# Revit family: 6180 series
name_source: partatom
category: Mechanical Equipment
revit_build: Autodesk Revit 2013 (Build: 20120221_2030(x64)
units: mm (PartAtom-declared; Revit-internal decimal feet)

## types (96) — shared parameters
Assembly Code = D2010900
Default Elevation = 0"
Description = Commercial Effluent Pumps
Discharge Height = 6"
Height = 21 3/16"
Hertz = 60
Impeller Type = Bronze Vortex
Installation Type = Floor Mounted
Length = 12 3/4"
Manufacturer = Zoeller
Masterformat Number = 33 36 16
Masterformat Title = Utility Septic Tank Effluent Pumps
Material = Cast Iron-Zoeller-Powder Coated Epoxy
Max. Water Temp. = 130 °F
Min. Recommended Fluid Level = 10"
Moisture Sensor (Optional) = Requires a circuit in control panel
Motor Design Letter = NEMA B
Motor Shaft = 416 S.S.
Motor Thermal Shutoff (Single Phase Only) = Thermal Overload Protector With Automatic Reset.
Motor Type = Submersible
O-Rings and Cover Gasket = Viton
Omniclass Table 23 Code = 23.60.30.21
Omniclass Table 23 Title = Pumps
Operation = Non-Automatic
Price = Prices may vary. Please consult Manufacturer Representative for most up-to-date price list.
Product Page URL = http://www.zoellerengprod.com
RPM = 3450
Service Factor = 1.15
Shaft Seal Lower (Options) = Silicon Carbide/Silicon Carbide
Shaft Seal Lower Standard = Silicon Carbide/Carbon
Shaft Seal Upper (Options) = Silicon Carbide/Carbon, Silicon Carbide/Silicon Carbide
Shaft Seal Upper Standard = Carbon/Ceramic
Shipping Weight = 89-94 lbs
Type SOW Power Cord Length = 300"
URL = http://www.zoellerengprod.com
Warranty Information = 36 Months (Limited)
Waste Connection = Yes
Width = 8"

## per-type parameters (varying)
| type | Apparent power | Discharge Diameter | Discharge Radius | Flange | Flange Visibility Height | Flow 6185 @ 30', 6186, 6188, 6189 @ 5' | Full Load Amps | Insulation | Lead Wires Insulation | Locked Rotor Amps (Voltage Dependant) | Max. Stator Temp. | Maximum Head | Minimum Head | Model | Motor | No Flange | Phase | Type | Void Visibility | Voltage |
| 6185-1.5" 200V 1Ph | 2300 VA | 1-1/2" NPT | 3/4" | No | 5 1/2" | 85 GPM | 12 A | Class B | Class B | 26.9 | 266 °F | 876" | 360" | 6185-1.5" | 1 HP | Yes | 1 | Permanent Split Capacitor | 8 1/4" | 200 V |
| 6185-1.5" 208V 1Ph | 2392 VA | 1-1/2" NPT | 3/4" | No | 5 1/2" | 85 GPM | 12 A | Class B | Class B | 26.9 | 266 °F | 876" | 360" | 6185-1.5" | 1 HP | Yes | 1 | Permanent Split Capacitor | 8 1/4" | 208 V |
| 6185-1.5" 230V 1Ph | 2254 VA | 1-1/2" NPT | 3/4" | No | 5 1/2" | 85 GPM | 10 A | Class B | Class B | 19.0 | 266 °F | 876" | 360" | 6185-1.5" | 1 HP | Yes | 1 | Permanent Split Capacitor | 8 1/4" | 230 V |
| 6185-1.5" 200V 3Ph | 1500 VA | 1-1/2" NPT | 3/4" | No | 5 1/2" | 85 GPM | 8 A | Class B | Class B | 30.0 | 266 °F | 876" | 360" | 6185-1.5" | 1 HP | Yes | 3 | 3 Phase | 8 1/4" | 200 V |
| 6185-1.5" 208V 3Ph | 1560 VA | 1-1/2" NPT | 3/4" | No | 5 1/2" | 85 GPM | 8 A | Class B | Class B | 30.0 | 266 °F | 876" | 360" | 6185-1.5" | 1 HP | Yes | 3 | 3 Phase | 8 1/4" | 208 V |
| 6185-1.5" 230V 3Ph | 1702 VA | 1-1/2" NPT | 3/4" | No | 5 1/2" | 85 GPM | 7 A | Class B | Class B | 27.0 | 266 °F | 876" | 360" | 6185-1.5" | 1 HP | Yes | 3 | 3 Phase | 8 1/4" | 230 V |
| 6185-1.5" 460V 3Ph | 1702 VA | 1-1/2" NPT | 3/4" | No | 5 1/2" | 85 GPM | 4 A | Class B | Class B | 14.0 | 266 °F | 876" | 360" | 6185-1.5" | 1 HP | Yes | 3 | 3 Phase | 8 1/4" | 460 V |
| 6185-1.5" 575V 3Ph | 1898 VA | 1-1/2" NPT | 3/4" | No | 5 1/2" | 85 GPM | 3 A | Class B | Class B | 12.0 | 266 °F | 876" | 360" | 6185-1.5" | 1 HP | Yes | 3 | 3 Phase | 8 1/4" | 575 V |
| 6185-2" 200V 1Ph | 2300 VA | 2" NPT | 1" | Yes | 6" | 85 GPM | 12 A | Class B | Class B | 26.9 | 266 °F | 876" | 360" | 6185-2" | 1 HP | No | 1 | Permanent Split Capacitor | 3" | 200 V |
| 6185-2" 208V 1Ph | 2392 VA | 2" NPT | 1" | Yes | 6" | 85 GPM | 12 A | Class B | Class B | 26.9 | 266 °F | 876" | 360" | 6185-2" | 1 HP | No | 1 | Permanent Split Capacitor | 3" | 208 V |
| 6185-2" 230V 1Ph | 2254 VA | 2" NPT | 1" | Yes | 6" | 85 GPM | 10 A | Class B | Class B | 19.0 | 266 °F | 876" | 360" | 6185-2" | 1 HP | No | 1 | Permanent Split Capacitor | 3" | 230 V |
| 6185-2" 200V 3Ph | 1500 VA | 2" NPT | 1" | Yes | 6" | 85 GPM | 8 A | Class B | Class B | 30.0 | 266 °F | 876" | 360" | 6185-2" | 1 HP | No | 3 | 3 Phase | 3" | 200 V |
| 6185-2" 208V 3Ph | 1560 VA | 2" NPT | 1" | Yes | 6" | 85 GPM | 8 A | Class B | Class B | 30.0 | 266 °F | 876" | 360" | 6185-2" | 1 HP | No | 3 | 3 Phase | 3" | 208 V |
| 6185-2" 230V 3Ph | 1702 VA | 2" NPT | 1" | Yes | 6" | 85 GPM | 7 A | Class B | Class B | 27.0 | 266 °F | 876" | 360" | 6185-2" | 1 HP | No | 3 | 3 Phase | 3" | 230 V |
| 6185-2" 460V 3Ph | 1702 VA | 2" NPT | 1" | Yes | 6" | 85 GPM | 4 A | Class B | Class B | 14.0 | 266 °F | 876" | 360" | 6185-2" | 1 HP | No | 3 | 3 Phase | 3" | 460 V |
| 6185-2" 575V 3Ph | 1898 VA | 2" NPT | 1" | Yes | 6" | 85 GPM | 3 A | Class B | Class B | 12.0 | 266 °F | 876" | 360" | 6185-2" | 1 HP | No | 3 | 3 Phase | 3" | 575 V |
| 6185-3" 200V 1Ph | 2300 VA | 3" NPT | 1 1/2" | Yes | 6" | 85 GPM | 12 A | Class B | Class B | 26.9 | 266 °F | 876" | 360" | 6185-3" | 1 HP | No | 1 | Permanent Split Capacitor | 3" | 200 V |
| 6185-3" 208V 1Ph | 2392 VA | 3" NPT | 1 1/2" | Yes | 6" | 85 GPM | 12 A | Class B | Class B | 26.9 | 266 °F | 876" | 360" | 6185-3" | 1 HP | No | 1 | Permanent Split Capacitor | 3" | 208 V |
| 6185-3" 230V 1Ph | 2254 VA | 3" NPT | 1 1/2" | Yes | 6" | 85 GPM | 10 A | Class B | Class B | 19.0 | 266 °F | 876" | 360" | 6185-3" | 1 HP | No | 1 | Permanent Split Capacitor | 3" | 230 V |
| 6185-3" 200V 3Ph | 1500 VA | 3" NPT | 1 1/2" | Yes | 6" | 85 GPM | 8 A | Class B | Class B | 30.0 | 266 °F | 876" | 360" | 6185-3" | 1 HP | No | 3 | 3 Phase | 3" | 200 V |
| 6185-3" 208V 3Ph | 1560 VA | 3" NPT | 1 1/2" | Yes | 6" | 85 GPM | 8 A | Class B | Class B | 30.0 | 266 °F | 876" | 360" | 6185-3" | 1 HP | No | 3 | 3 Phase | 3" | 208 V |
| 6185-3" 230V 3Ph | 1702 VA | 3" NPT | 1 1/2" | Yes | 6" | 85 GPM | 7 A | Class B | Class B | 27.0 | 266 °F | 876" | 360" | 6185-3" | 1 HP | No | 3 | 3 Phase | 3" | 230 V |
| 6185-3" 460V 3Ph | 1702 VA | 3" NPT | 1 1/2" | Yes | 6" | 85 GPM | 4 A | Class B | Class B | 14.0 | 266 °F | 876" | 360" | 6185-3" | 1 HP | No | 3 | 3 Phase | 3" | 460 V |
| 6185-3" 575V 3Ph | 1898 VA | 3" NPT | 1 1/2" | Yes | 6" | 85 GPM | 3 A | Class B | Class B | 12.0 | 266 °F | 876" | 360" | 6185-3" | 1 HP | No | 3 | 3 Phase | 3" | 575 V |
| 6186-1.5" 200V 1Ph | 3440 VA | 1-1/2" NPT | 3/4" | No | 5 1/2" | 58 GPM | 17 A | Class F | Class F | 48.3 | 311 °F | 1368" | 60" | 6186-1.5" | 1-1/2 HP | Yes | 1 | Permanent Split Capacitor | 8 1/4" | 200 V |
| 6186-1.5" 208V 1Ph | 3578 VA | 1-1/2" NPT | 3/4" | No | 5 1/2" | 58 GPM | 17 A | Class F | Class F | 48.3 | 311 °F | 1368" | 60" | 6186-1.5" | 1-1/2 HP | Yes | 1 | Permanent Split Capacitor | 8 1/4" | 208 V |
| 6186-1.5" 230V 1Ph | 3151 VA | 1-1/2" NPT | 3/4" | No | 5 1/2" | 58 GPM | 14 A | Class F | Class F | 38.0 | 311 °F | 1368" | 60" | 6186-1.5" | 1-1/2 HP | Yes | 1 | Permanent Split Capacitor | 8 1/4" | 230 V |
| 6186-1.5" 200V 3Ph | 2060 VA | 1-1/2" NPT | 3/4" | No | 5 1/2" | 58 GPM | 10 A | Class F | Class F | 42.0 | 311 °F | 1368" | 60" | 6186-1.5" | 1-1/2 HP | Yes | 3 | 3 Phase | 8 1/4" | 200 V |
| 6186-1.5" 208V 3Ph | 2142 VA | 1-1/2" NPT | 3/4" | No | 5 1/2" | 58 GPM | 10 A | Class F | Class F | 42.0 | 311 °F | 1368" | 60" | 6186-1.5" | 1-1/2 HP | Yes | 3 | 3 Phase | 8 1/4" | 208 V |
| 6186-1.5" 230V 3Ph | 2254 VA | 1-1/2" NPT | 3/4" | No | 5 1/2" | 58 GPM | 10 A | Class F | Class F | 35.0 | 311 °F | 1368" | 60" | 6186-1.5" | 1-1/2 HP | Yes | 3 | 3 Phase | 8 1/4" | 230 V |
| 6186-1.5" 460V 3Ph | 2116 VA | 1-1/2" NPT | 3/4" | No | 5 1/2" | 58 GPM | 5 A | Class F | Class F | 18.0 | 311 °F | 1368" | 60" | 6186-1.5" | 1-1/2 HP | Yes | 3 | 3 Phase | 8 1/4" | 460 V |
| 6186-1.5" 575V 3Ph | 2070 VA | 1-1/2" NPT | 3/4" | No | 5 1/2" | 58 GPM | 4 A | Class F | Class F | 18.0 | 311 °F | 1368" | 60" | 6186-1.5" | 1-1/2 HP | Yes | 3 | 3 Phase | 8 1/4" | 575 V |
| 6186-2" 200V 1Ph | 3440 VA | 2" NPT | 1" | Yes | 6" | 58 GPM | 17 A | Class F | Class F | 48.3 | 311 °F | 1368" | 60" | 6186-2" | 1-1/2 HP | No | 1 | Permanent Split Capacitor | 3" | 200 V |
| 6186-2" 208V 1Ph | 3578 VA | 2" NPT | 1" | Yes | 6" | 58 GPM | 17 A | Class F | Class F | 48.3 | 311 °F | 1368" | 60" | 6186-2" | 1-1/2 HP | No | 1 | Permanent Split Capacitor | 3" | 208 V |
| 6186-2" 230V 1Ph | 3151 VA | 2" NPT | 1" | Yes | 6" | 58 GPM | 14 A | Class F | Class F | 38.0 | 311 °F | 1368" | 60" | 6186-2" | 1-1/2 HP | No | 1 | Permanent Split Capacitor | 3" | 230 V |
| 6186-2" 200V 3Ph | 2060 VA | 2" NPT | 1" | Yes | 6" | 58 GPM | 10 A | Class F | Class F | 42.0 | 311 °F | 1368" | 60" | 6186-2" | 1-1/2 HP | No | 3 | 3 Phase | 3" | 200 V |
| 6186-2" 208V 3Ph | 2142 VA | 2" NPT | 1" | Yes | 6" | 58 GPM | 10 A | Class F | Class F | 42.0 | 311 °F | 1368" | 60" | 6186-2" | 1-1/2 HP | No | 3 | 3 Phase | 3" | 208 V |
| 6186-2" 230V 3Ph | 2116 VA | 2" NPT | 1" | Yes | 6" | 58 GPM | 9 A | Class F | Class F | 35.0 | 311 °F | 1368" | 60" | 6186-2" | 1-1/2 HP | No | 3 | 3 Phase | 3" | 230 V |
| 6186-2" 460V 3Ph | 2116 VA | 2" NPT | 1" | Yes | 6" | 58 GPM | 5 A | Class F | Class F | 18.0 | 311 °F | 1368" | 60" | 6186-2" | 1-1/2 HP | No | 3 | 3 Phase | 3" | 460 V |
| 6186-2" 575V 3Ph | 2070 VA | 2" NPT | 1" | Yes | 6" | 58 GPM | 4 A | Class F | Class F | 18.0 | 311 °F | 1368" | 60" | 6186-2" | 1-1/2 HP | No | 3 | 3 Phase | 3" | 575 V |
| 6186-3" 200V 1Ph | 3440 VA | 3" NPT | 1 1/2" | Yes | 6" | 58 GPM | 17 A | Class F | Class F | 48.3 | 311 °F | 1368" | 60" | 6186-3" | 1-1/2 HP | No | 1 | Permanent Split Capacitor | 3" | 200 V |
| 6186-3" 208V 1Ph | 3578 VA | 3" NPT | 1 1/2" | Yes | 6" | 58 GPM | 17 A | Class F | Class F | 48.3 | 311 °F | 1368" | 60" | 6186-3" | 1-1/2 HP | No | 1 | Permanent Split Capacitor | 3" | 208 V |
| 6186-3" 230V 1Ph | 3151 VA | 3" NPT | 1 1/2" | Yes | 6" | 58 GPM | 14 A | Class F | Class F | 38.0 | 311 °F | 1368" | 60" | 6186-3" | 1-1/2 HP | No | 1 | Permanent Split Capacitor | 3" | 230 V |
| 6186-3" 200V 3Ph | 2060 VA | 3" NPT | 1 1/2" | Yes | 6" | 58 GPM | 10 A | Class F | Class F | 42.0 | 311 °F | 1368" | 60" | 6186-3" | 1-1/2 HP | No | 3 | 3 Phase | 3" | 200 V |
| 6186-3" 208V 3Ph | 2142 VA | 3" NPT | 1 1/2" | Yes | 6" | 58 GPM | 10 A | Class F | Class F | 42.0 | 311 °F | 1368" | 60" | 6186-3" | 1-1/2 HP | No | 3 | 3 Phase | 3" | 208 V |
| 6186-3" 230V 3Ph | 2116 VA | 3" NPT | 1 1/2" | Yes | 6" | 58 GPM | 9 A | Class F | Class F | 35.0 | 311 °F | 1368" | 60" | 6186-3" | 1-1/2 HP | No | 3 | 3 Phase | 3" | 230 V |
| 6186-3" 460V 3Ph | 2116 VA | 3" NPT | 1 1/2" | Yes | 6" | 58 GPM | 5 A | Class F | Class F | 18.0 | 311 °F | 1368" | 60" | 6186-3" | 1-1/2 HP | No | 3 | 3 Phase | 3" | 460 V |
| 6186-3" 575V 3Ph | 2070 VA | 3" NPT | 1 1/2" | Yes | 6" | 58 GPM | 4 A | Class F | Class F | 18.0 | 311 °F | 1368" | 60" | 6186-3" | 1-1/2 HP | No | 3 | 3 Phase | 3" | 575 V |
| 6188-1.5" 200V 1Ph | 3360 VA | 1-1/2" NPT | 3/4" | No | 5 1/2" | 145 GPM | 17 A | Class F | Class F | 48.3 | 311 °F | 1092" | 60" | 6188-1.5" | 1-1/2 HP | Yes | 1 | Permanent Split Capacitor | 8 1/4" | 200 V |
| 6188-1.5" 208V 1Ph | 3494 VA | 1-1/2" NPT | 3/4" | No | 5 1/2" | 145 GPM | 17 A | Class F | Class F | 48.3 | 311 °F | 1092" | 60" | 6188-1.5" | 1-1/2 HP | Yes | 1 | Permanent Split Capacitor | 8 1/4" | 208 V |
| 6188-1.5" 230V 1Ph | 3220 VA | 1-1/2" NPT | 3/4" | No | 5 1/2" | 145 GPM | 14 A | Class F | Class F | 38.0 | 311 °F | 1092" | 60" | 6188-1.5" | 1-1/2 HP | Yes | 1 | Permanent Split Capacitor | 8 1/4" | 230 V |
| 6188-1.5" 200V 3Ph | 2060 VA | 1-1/2" NPT | 3/4" | No | 5 1/2" | 145 GPM | 10 A | Class F | Class F | 42.0 | 311 °F | 1092" | 60" | 6188-1.5" | 1-1/2 HP | Yes | 3 | 3 Phase | 8 1/4" | 200 V |
| 6188-1.5" 208V 3Ph | 2142 VA | 1-1/2" NPT | 3/4" | No | 5 1/2" | 145 GPM | 10 A | Class F | Class F | 42.0 | 311 °F | 1092" | 60" | 6188-1.5" | 1-1/2 HP | Yes | 3 | 3 Phase | 8 1/4" | 208 V |
| 6188-1.5" 230V 3Ph | 2047 VA | 1-1/2" NPT | 3/4" | No | 5 1/2" | 145 GPM | 9 A | Class F | Class F | 35.0 | 311 °F | 1092" | 60" | 6188-1.5" | 1-1/2 HP | Yes | 3 | 3 Phase | 8 1/4" | 230 V |
| 6188-1.5" 460V 3Ph | 2116 VA | 1-1/2" NPT | 3/4" | No | 5 1/2" | 145 GPM | 5 A | Class F | Class F | 18.0 | 311 °F | 1092" | 60" | 6188-1.5" | 1-1/2 HP | Yes | 3 | 3 Phase | 8 1/4" | 460 V |
| 6188-1.5" 575V 3Ph | 2013 VA | 1-1/2" NPT | 3/4" | No | 5 1/2" | 145 GPM | 4 A | Class F | Class F | 18.0 | 311 °F | 1092" | 60" | 6188-1.5" | 1-1/2 HP | Yes | 3 | 3 Phase | 8 1/4" | 575 V |
| 6188-2" 200V 1Ph | 3360 VA | 2" NPT | 1" | Yes | 6" | 145 GPM | 17 A | Class F | Class F | 48.3 | 311 °F | 1092" | 60" | 6188-2" | 1-1/2 HP | No | 1 | Permanent Split Capacitor | 3" | 200 V |
| 6188-2" 208V 1Ph | 3494 VA | 2" NPT | 1" | Yes | 6" | 145 GPM | 17 A | Class F | Class F | 48.3 | 311 °F | 1092" | 60" | 6188-2" | 1-1/2 HP | No | 1 | Permanent Split Capacitor | 3" | 208 V |
| 6188-2" 230V 1Ph | 3220 VA | 2" NPT | 1" | Yes | 6" | 145 GPM | 14 A | Class F | Class F | 38 | 311 °F | 1092" | 60" | 6188-2" | 1-1/2 HP | No | 1 | Permanent Split Capacitor | 3" | 230 V |
| 6188-2" 200V 3Ph | 2060 VA | 2" NPT | 1" | Yes | 6" | 145 GPM | 10 A | Class F | Class F | 42.0 | 311 °F | 1092" | 60" | 6188-2" | 1-1/2 HP | No | 3 | 3 Phase | 3" | 200 V |
| 6188-2" 208V 3Ph | 2142 VA | 2" NPT | 1" | Yes | 6" | 145 GPM | 10 A | Class F | Class F | 42.0 | 311 °F | 1092" | 60" | 6188-2" | 1-1/2 HP | No | 3 | 3 Phase | 3" | 208 V |
| 6188-2" 230V 3Ph | 2047 VA | 2" NPT | 1" | Yes | 6" | 145 GPM | 9 A | Class F | Class F | 35.0 | 311 °F | 1092" | 60" | 6188-2" | 1-1/2 HP | No | 3 | 3 Phase | 3" | 230 V |
| 6188-2" 460V 3Ph | 2116 VA | 2" NPT | 1" | Yes | 6" | 145 GPM | 5 A | Class F | Class F | 18.0 | 311 °F | 1092" | 60" | 6188-2" | 1-1/2 HP | No | 3 | 3 Phase | 3" | 460 V |
| 6188-2" 575V 3Ph | 2013 VA | 2" NPT | 1" | Yes | 6" | 145 GPM | 4 A | Class F | Class F | 18.0 | 311 °F | 1092" | 60" | 6188-2" | 1-1/2 HP | No | 3 | 3 Phase | 3" | 575 V |
| 6188-3" 200V 1Ph | 3360 VA | 3" NPT | 1 1/2" | Yes | 6" | 145 GPM | 17 A | Class F | Class F | 48.3 | 311 °F | 1092" | 60" | 6188-3" | 1-1/2 HP | No | 1 | Permanent Split Capacitor | 3" | 200 V |
| 6188-3" 208V 1Ph | 3494 VA | 3" NPT | 1 1/2" | Yes | 6" | 145 GPM | 17 A | Class F | Class F | 48.3 | 311 °F | 1092" | 60" | 6188-3" | 1-1/2 HP | No | 1 | Permanent Split Capacitor | 3" | 208 V |
| 6188-3" 230V 1Ph | 3220 VA | 3" NPT | 1 1/2" | Yes | 6" | 145 GPM | 14 A | Class F | Class F | 38.0 | 311 °F | 1092" | 60" | 6188-3" | 1-1/2 HP | No | 1 | Permanent Split Capacitor | 3" | 230 V |
| 6188-3" 200V 3Ph | 2060 VA | 3" NPT | 1 1/2" | Yes | 6" | 145 GPM | 10 A | Class F | Class F | 38.0 | 311 °F | 1092" | 60" | 6188-3" | 1-1/2 HP | No | 3 | 3 Phase | 3" | 200 V |
| 6188-3" 208V 3Ph | 2142 VA | 3" NPT | 1 1/2" | Yes | 6" | 145 GPM | 10 A | Class F | Class F | 38.0 | 311 °F | 1092" | 60" | 6188-3" | 1-1/2 HP | No | 3 | 3 Phase | 3" | 208 V |
| 6188-3" 230V 3Ph | 2047 VA | 3" NPT | 1 1/2" | Yes | 6" | 145 GPM | 9 A | Class F | Class F | 35.0 | 311 °F | 1092" | 60" | 6188-3" | 1-1/2 HP | No | 3 | 3 Phase | 3" | 230 V |
| 6188-3" 460V 3Ph | 2116 VA | 3" NPT | 1 1/2" | Yes | 6" | 145 GPM | 5 A | Class F | Class F | 18.0 | 311 °F | 1092" | 60" | 6188-3" | 1-1/2 HP | No | 3 | 3 Phase | 3" | 460 V |
| 6188-3" 575V 3Ph | 2013 VA | 3" NPT | 1 1/2" | Yes | 6" | 145 GPM | 4 A | Class F | Class F | 18.0 | 311 °F | 1092" | 60" | 6188-3" | 1-1/2 HP | No | 3 | 3 Phase | 3" | 575 V |
| 6189-1.5" 200V 1Ph | 4100 VA | 1-1/2" NPT | 3/4" | No | 5 1/2" | 145 GPM | 21 A | Class F | Class F | 48.3 | 266 °F | 1320" | 60" | 6189-1.5" | 2 HP | Yes | 1 | Permanent Split Capacitor | 8 1/4" | 200 V |
| 6189-1.5" 208V 1Ph | 4264 VA | 1-1/2" NPT | 3/4" | No | 5 1/2" | 145 GPM | 21 A | Class F | Class F | 48.3 | 266 °F | 1320" | 60" | 6189-1.5" | 2 HP | Yes | 1 | Permanent Split Capacitor | 8 1/4" | 208 V |
| 6189-1.5" 230V 1Ph | 3933 VA | 1-1/2" NPT | 3/4" | No | 5 1/2" | 145 GPM | 17 A | Class F | Class F | 38.0 | 266 °F | 1320" | 60" | 6189-1.5" | 2 HP | Yes | 1 | Permanent Split Capacitor | 8 1/4" | 230 V |
| 6189-1.5" 200V 3Ph | 2640 VA | 1-1/2" NPT | 3/4" | No | 5 1/2" | 145 GPM | 13 A | Class F | Class F | 42.0 | 266 °F | 1320" | 60" | 6189-1.5" | 2 HP | Yes | 3 | 3 Phase | 8 1/4" | 200 V |
| 6189-1.5" 208V 3Ph | 2746 VA | 1-1/2" NPT | 3/4" | No | 5 1/2" | 145 GPM | 13 A | Class F | Class F | 42.0 | 266 °F | 1320" | 60" | 6189-1.5" | 2 HP | Yes | 3 | 3 Phase | 8 1/4" | 208 V |
| 6189-1.5" 230V 3Ph | 2576 VA | 1-1/2" NPT | 3/4" | No | 5 1/2" | 145 GPM | 11 A | Class F | Class F | 35.0 | 266 °F | 1320" | 60" | 6189-1.5" | 2 HP | Yes | 3 | 3 Phase | 8 1/4" | 230 V |
| 6189-1.5" 460V 3Ph | 2760 VA | 1-1/2" NPT | 3/4" | No | 5 1/2" | 145 GPM | 6 A | Class F | Class F | 18.0 | 266 °F | 1320" | 60" | 6189-1.5" | 2 HP | Yes | 3 | 3 Phase | 8 1/4" | 460 V |
| 6189-1.5" 575V 3Ph | 3335 VA | 1-1/2" NPT | 3/4" | No | 5 1/2" | 145 GPM | 6 A | Class F | Class F | 18.0 | 266 °F | 1320" | 60" | 6189-1.5" | 2 HP | Yes | 3 | 3 Phase | 8 1/4" | 575 V |
| 6189-2" 200V 1Ph | 4100 VA | 2" NPT | 1" | Yes | 6" | 145 GPM | 21 A | Class F | Class F | 48.3 | 266 °F | 1320" | 60" | 6189-2" | 2 HP | No | 1 | Permanent Split Capacitor | 3" | 200 V |
| 6189-2" 208V 1Ph | 4264 VA | 2" NPT | 1" | Yes | 6" | 145 GPM | 21 A | Class F | Class F | 48.3 | 266 °F | 1320" | 60" | 6189-2" | 2 HP | No | 1 | Permanent Split Capacitor | 3" | 208 V |
| 6189-2" 230V 1Ph | 3933 VA | 2" NPT | 1" | Yes | 6" | 145 GPM | 17 A | Class F | Class F | 38.0 | 266 °F | 1320" | 60" | 6189-2" | 2 HP | No | 1 | Permanent Split Capacitor | 3" | 230 V |
| 6189-2" 200V 3Ph | 2640 VA | 2" NPT | 1" | Yes | 6" | 145 GPM | 13 A | Class F | Class F | 42.0 | 266 °F | 1320" | 60" | 6189-2" | 2 HP | No | 3 | 3 Phase | 3" | 200 V |
| 6189-2" 208V 3Ph | 2746 VA | 2" NPT | 1" | Yes | 6" | 145 GPM | 13 A | Class F | Class F | 42.0 | 266 °F | 1320" | 60" | 6189-2" | 2 HP | No | 3 | 3 Phase | 3" | 208 V |
| 6189-2" 230V 3Ph | 2576 VA | 2" NPT | 1" | Yes | 6" | 145 GPM | 11 A | Class F | Class F | 35.0 | 266 °F | 1320" | 60" | 6189-2" | 2 HP | No | 3 | 3 Phase | 3" | 230 V |
| 6189-2" 460V 3Ph | 2760 VA | 2" NPT | 1" | Yes | 6" | 145 GPM | 6 A | Class F | Class F | 18.0 | 266 °F | 1320" | 60" | 6189-2" | 2 HP | No | 3 | 3 Phase | 3" | 460 V |
| 6189-2" 575V 3Ph | 3335 VA | 2" NPT | 1" | Yes | 6" | 145 GPM | 6 A | Class F | Class F | 18.0 | 266 °F | 1320" | 60" | 6189-2" | 2 HP | No | 3 | 3 Phase | 3" | 575 V |
| 6189-3" 200V 1Ph | 4100 VA | 3" NPT | 1 1/2" | Yes | 6" | 145 GPM | 21 A | Class F | Class F | 48.3 | 266 °F | 1320" | 60" | 6189-3" | 2 HP | No | 1 | Permanent Split Capacitor | 3" | 200 V |
| 6189-3" 208V 1Ph | 4264 VA | 3" NPT | 1 1/2" | Yes | 6" | 145 GPM | 21 A | Class F | Class F | 48.3 | 266 °F | 1320" | 60" | 6189-3" | 2 HP | No | 1 | Permanent Split Capacitor | 3" | 208 V |
| 6189-3" 230V 1Ph | 3933 VA | 3" NPT | 1 1/2" | Yes | 6" | 145 GPM | 17 A | Class F | Class F | 38.0 | 266 °F | 1320" | 60" | 6189-3" | 2 HP | No | 1 | Permanent Split Capacitor | 3" | 230 V |
| 6189-3" 200V 3Ph | 2640 VA | 3" NPT | 1 1/2" | Yes | 6" | 145 GPM | 13 A | Class F | Class F | 42.0 | 266 °F | 1320" | 60" | 6189-3" | 2 HP | No | 3 | 3 Phase | 3" | 200 V |
| 6189-3" 208V 3Ph | 2746 VA | 3" NPT | 1 1/2" | Yes | 6" | 145 GPM | 13 A | Class F | Class F | 42.0 | 266 °F | 1320" | 60" | 6189-3" | 2 HP | No | 3 | 3 Phase | 3" | 208 V |
| 6189-3" 230V 3Ph | 2576 VA | 3" NPT | 1 1/2" | Yes | 6" | 145 GPM | 11 A | Class F | Class F | 35.0 | 266 °F | 1320" | 60" | 6189-3" | 2 HP | No | 3 | 3 Phase | 3" | 230 V |
| 6189-3" 460V 3Ph | 2760 VA | 3" NPT | 1 1/2" | Yes | 6" | 145 GPM | 6 A | Class F | Class F | 18.0 | 266 °F | 1320" | 60" | 6189-3" | 2 HP | No | 3 | 3 Phase | 3" | 460 V |
| 6189-3" 575V 3Ph | 3335 VA | 3" NPT | 1 1/2" | Yes | 6" | 145 GPM | 6 A | Class F | Class F | 18.0 | 266 °F | 1320" | 60" | 6189-3" | 2 HP | No | 3 | 3 Phase | 3" | 575 V |

## geometry (parser evidence)
native form markers: Blend x4, Sweep x2
no freeform markers — native parametric forms only
